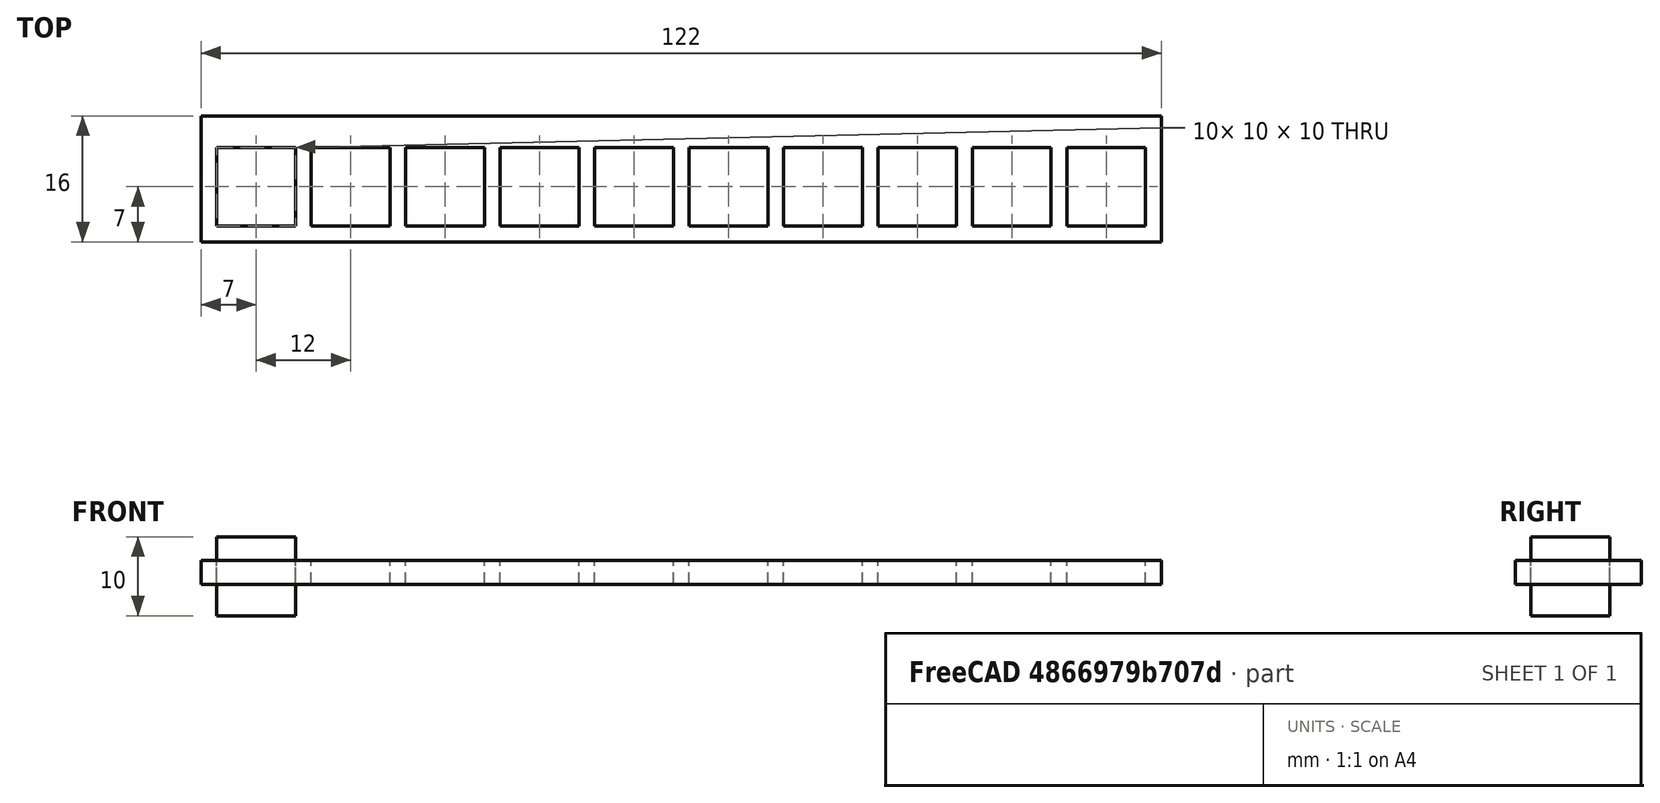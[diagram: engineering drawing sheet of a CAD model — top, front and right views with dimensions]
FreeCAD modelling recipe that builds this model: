
FCSTD DOCUMENT  (FreeCAD 0.21R33694 (Git))
Label: OJT1_T010p09_X
License: All rights reserved
LicenseURL: http://en.wikipedia.org/wiki/All_rights_reserved
objects: Part::Box×2, Part::FeaturePython×1, Part::Cut×1
note: 3 computed .brp shape members not serialized (recipe doc carries the construction recipe); baked Part::Feature solids carry a one-line shape summary decoded from their .brp

FEATURE [Part::Box] Box  label="Cube"
  AttacherType = Attacher::AttachEngine3D
  Height = 10
  Length = 10
  Width = 10
FEATURE [Part::FeaturePython] Array  # Draft array (typed FeaturePython)
  AlwaysSyncPlacement = false
  Angle = 360
  ArrayType = 0
  Axis = (0,0,1)
  Base = -> Box
  Center = (0,0,0)
  Count = 10
  ExpandArray = false
  Fuse = false
  IntervalAxis = (0,0,0)
  IntervalX = (12,0,0)
  IntervalY = (0,100,0)
  IntervalZ = (0,0,100)
  NumberCircles = 3
  NumberPolar = 5
  NumberX = 10
  NumberY = 1
  NumberZ = 1
  PlacementList = 10 placements: arithmetic series from (0,0,0) step (12,0,0) to (108,0,0)
  RadialDistance = 50
  ScaleList = (10) [(1,1,1),(1,1,1),(1,1,1),(1,1,1),(1,1,1),(1,1,1),(1,1,1),(1,1,1),(1,1,1),(1,1,1)]
  Symmetry = 1
  TangentialDistance = 25
FEATURE [Part::Box] Box001  label="Cube001"
  AttacherType = Attacher::AttachEngine3D
  Height = 3
  Length = 122
  Placement = pos=(-2,-2,4) rot=(0,0,1;0rad)
  Width = 16
FEATURE [Part::Cut] Cut
  Base = -> Box001
  Refine = true
  Tool = -> Array
